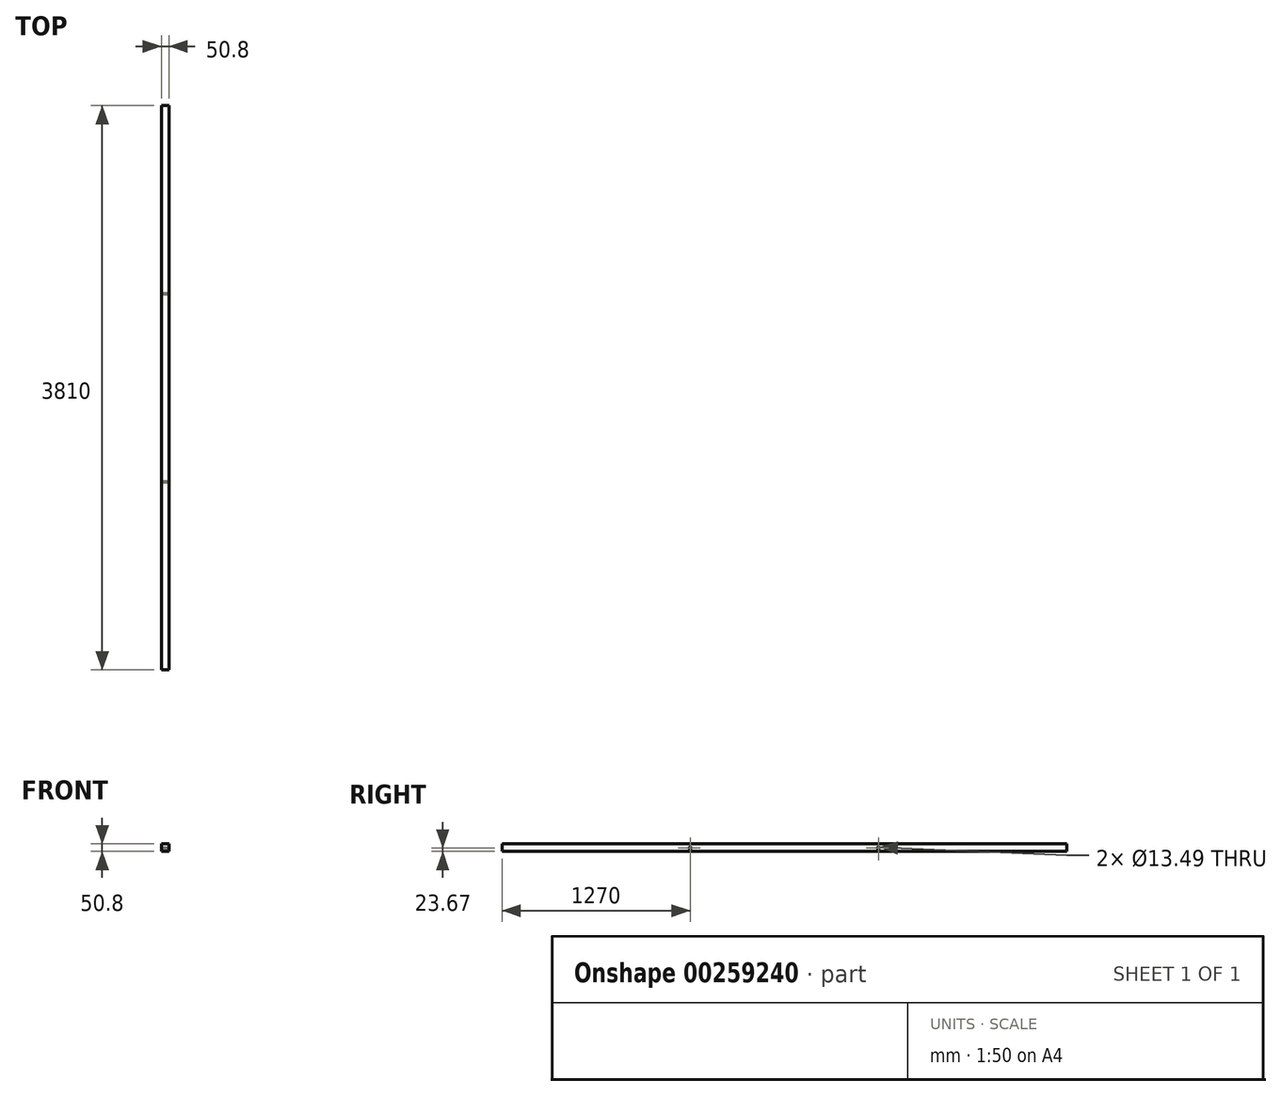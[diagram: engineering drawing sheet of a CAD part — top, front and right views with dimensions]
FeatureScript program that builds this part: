
annotation { "Feature Type Name" : "Feature", "Feature Type Description" : "" }
export const myFeature = defineFeature(function(context is Context, id is Id, definition is map)
    precondition{}
    {
        {
            var Q0;
            Q0=qCreatedBy(makeId("Front.planeOp"),FACE);
            var sketch = newSketch(context, id + "F0", { "sketchPlane" : qUnion([Q0])});
            skLineSegment(sketch, "E0.bottom", {"start": v(-25.82, 27.13) * mm, "end": v(24.98, 27.13) * mm});
            skLineSegment(sketch, "E0.top", {"start": v(-25.82, -23.67) * mm, "end": v(24.98, -23.67) * mm});
            skLineSegment(sketch, "E0.left", {"start": v(-25.82, 27.13) * mm, "end": v(-25.82, -23.67) * mm});
            skLineSegment(sketch, "E0.right", {"start": v(24.98, 27.13) * mm, "end": v(24.98, -23.67) * mm});
            skSolve(sketch);
        }
        {
            var Q0;
            Q0=makeQuery(id+"F0.imprint","IMPRINT",FACE,{"disambiguationData":[TD([[makeQuery(id+"F0.imprint","IMPRINT",EDGE,{"derivedFrom":sQuery(id+"F0.wireOp",EDGE,"E0.bottom")}),-1.0]])]});
            extrude(context, id + "F1", {"entities" : qUnion([Q0]), "depth" : 3810 * mm});
        }
        {
            var Q0;
            Q0=makeQuery(id+"F1.opExtrude","SWEPT_FACE",FACE,{"disambiguationData":[OSD([sQuery(id+"F0.wireOp",EDGE,"E0.right")])]});
            var sketch = newSketch(context, id + "F2", { "sketchPlane" : qUnion([Q0])});
            skLineSegment(sketch, "E1", {"start": v(-3810, 0) * mm, "end": v(-2540, 0) * mm});
            skLineSegment(sketch, "E2", {"start": v(-2540, 0) * mm, "end": v(-1270, 0) * mm});
            skCircle(sketch, "E3", {"center": v(-2540, 0) * mm, "radius": 12.7 * mm});
            skCircle(sketch, "E4", {"center": v(-1270, 0) * mm, "radius": 12.7 * mm});
            skSolve(sketch);
        }
        {
            var Q0;
            Q0=sQuery(id+"F2.wireOp",VERTEX,"E4.center");
            var Q1;
            Q1=sQuery(id+"F2.wireOp",VERTEX,"E3.center");
            var Q2;
            Q2=makeQuery(id+"F1.opExtrude","SWEPT_BODY",BODY,{"disambiguationData":[OSD([sQuery(id+"F0.wireOp",EDGE,"E0.bottom"),sQuery(id+"F0.wireOp",EDGE,"E0.top"),sQuery(id+"F0.wireOp",EDGE,"E0.left"),sQuery(id+"F0.wireOp",EDGE,"E0.right")])]});
            hole(context, id + "F3", {"style" : HoleStyle.SIMPLE, "endStyle" : HoleEndStyle.THROUGH, "standardTappedOrClearance" : lookupTablePath({ "standard" : "ANSI", "fit" : "Normal (ASME)", "size" : "1/2", "type" : "Clearance" }), "standardBlindInLast" : lookupTablePath({ "fit" : "Free", "standard" : "ANSI", "size" : "1/2", "type" : "Clearance" }), "holeDiameter" : 13.5 * mm, "tappedDepth" : 12.7 * mm, "tapClearance" : 3, "locations" : qUnion([Q0, Q1]), "scope" : qUnion([Q2])});
        }
    });
